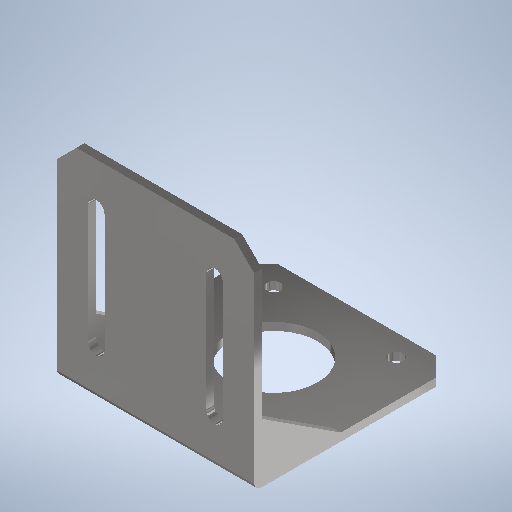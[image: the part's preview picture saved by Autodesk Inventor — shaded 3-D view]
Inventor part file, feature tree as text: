
AUTODESK INVENTOR PART (.ipt)
format: ipt  version: 2025.1 (Build 291241000, 241)  size: 322,560 bytes
history: native  units: mm
features: sketch x5, extrude x3, fillet x2, other x1, pattern_linear x1, hole x1
ambient origin geometry x8: Origin, YZ Plane, XZ Plane, XY Plane, X Axis, Y Axis, Z Axis, Center Point
bodies: Body1 (feature_tree)
feature tree (13):
  other  "Sólido1"
  sketch  "Boceto1"  dims[d0=50.0mm d1=51.0mm]
  extrude  "Extrusión1"  Depth=51.0mm
  extrude  "Extrusión2"  Depth=22.1mm
  extrude  "Extrusión3"  Depth=5.0mm
  pattern_linear  "Patrón rectangular1"  Spacing1=2.0mm  [1 undecoded]
  fillet  "Empalme1"  Radius=53.0mm
  fillet  "Empalme2"  Radius=4.2mm
  hole  "Hole1"  [1 undecoded]
  sketch  "Boceto2"  dims[d15=5.0mm d16=5.0mm]
  sketch  "Esboço - Padrão retangular1"  dims[d2=21.0mm d3=22.1mm]
  sketch  "Boceto3"  dims[d18=5.0mm d19=2.0mm d20=0.0mm d21=53.0mm d24=4.2mm d25=7.9mm d26=2.1mm d27=2.1mm d28=20.0mm d30=30.0mm d31=10.0mm d33=10.0mm d35=2.0mm d36=0.0mm d37=5.0mm d38=5.0mm d39=5.0mm d40=5.0mm d41=20.0mm d42=13.0mm d43=2.0mm d44=0.0mm d45=20.0mm d47=48.0mm d48=2.0mm d49=2.0mm d50=15.5mm d51=15.5mm d52=20.0mm d54=31.0mm d55=20.0mm d57=31.0mm d60=3.5mm d61=6.0mm d62=3.023mm d63=2.0mm d64=14.3117mm d65=8.0mm d66=20.594885mm d67=30.0mm d68=11.0mm]
  sketch  "Esboço - Padrão retangular2"  dims[d17=5.0mm]
note: 2 required parameter values undecoded (feature->parameter linkage not recoverable at this tier; creation-order binding heuristic only, values carry confidence <= 0.55)
